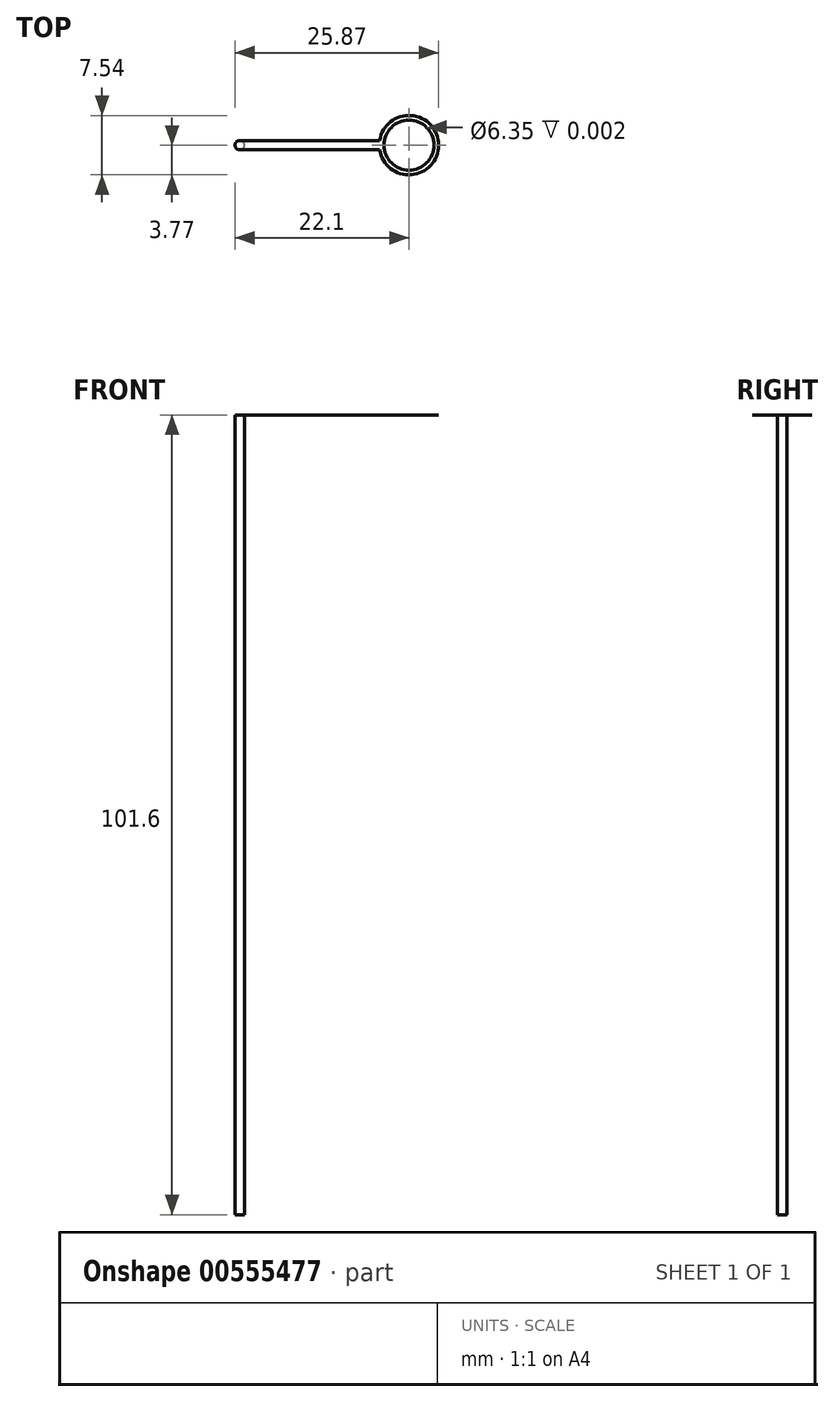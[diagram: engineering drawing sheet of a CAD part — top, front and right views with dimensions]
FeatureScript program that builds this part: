
annotation { "Feature Type Name" : "Feature", "Feature Type Description" : "" }
export const myFeature = defineFeature(function(context is Context, id is Id, definition is map)
    precondition{}
    {
        {
            var Q0;
            Q0=qCreatedBy(makeId("Top.planeOp"),FACE);
            var sketch = newSketch(context, id + "F0", { "sketchPlane" : qUnion([Q0])});
            skCircle(sketch, "E0", {"center": v(0, 0) * mm, "radius": 3.18 * mm});
            skCircle(sketch, "E1", {"center": v(0, 0) * mm, "radius": 3.77 * mm});
            skLineSegment(sketch, "E2", {"start": v(-21.5, 0.6) * mm, "end": v(-3.72, 0.6) * mm});
            skLineSegment(sketch, "E3", {"start": v(-21.5, -0.6) * mm, "end": v(-3.72, -0.6) * mm});
            skCircle(sketch, "E4", {"center": v(-21.5, 0) * mm, "radius": 0.6 * mm});
            skSolve(sketch);
        }
        {
            var Q0;
            {var subQ0=sQuery(id+"F0.wireOp",EDGE,"E2");Q0=makeQuery(id+"F0.imprint","IMPRINT",FACE,{"disambiguationData":[TD([[makeQuery(id+"F0.imprint","IMPRINT",EDGE,{"derivedFrom":subQ0}),-1.0]])]});}
            var Q1;
            Q1=makeQuery(id+"F0.imprint","IMPRINT",FACE,{"disambiguationData":[TD([[makeQuery(id+"F0.imprint","IMPRINT",EDGE,{"derivedFrom":sQuery(id+"F0.wireOp",EDGE,"E0")}),-1.0]])]});
            var Q2;
            {var subQ0=sQuery(id+"F0.wireOp",EDGE,"E4");var subQ1=makeQuery(id+"F0.imprint","INTERSECT",VERTEX,{"derivedFrom":[sQuery(id+"F0.wireOp",EDGE,"E2"),subQ0]});Q2=makeQuery(id+"F0.imprint","IMPRINT",FACE,{"disambiguationData":[TD([[makeQuery(id+"F0.imprint","IMPRINT",EDGE,{"disambiguationData":[TD([[subQ1,-1.0]])],"derivedFrom":subQ0}),1.0]])]});}
            extrude(context, id + "F1", {"entities" : qUnion([Q0, Q1, Q2]), "depth" : 3 / 1625.6 * mm, "offsetDistance" : 25.4 * mm});
        }
        {
            var Q0;
            {var subQ0=sQuery(id+"F0.wireOp",EDGE,"E4");var subQ1=makeQuery(id+"F0.imprint","INTERSECT",VERTEX,{"derivedFrom":[sQuery(id+"F0.wireOp",EDGE,"E2"),subQ0]});Q0=makeQuery(id+"F0.imprint","IMPRINT",FACE,{"disambiguationData":[TD([[makeQuery(id+"F0.imprint","IMPRINT",EDGE,{"disambiguationData":[TD([[subQ1,-1.0]])],"derivedFrom":subQ0}),1.0]])]});}
            var Q1;
            Q1=sQuery(id+"F0.wireOp",EDGE,"8kEqgfxY-QX5D-swLe-gkhk-hIvBlWavA6Kc");
            extrude(context, id + "F2", {"entities" : qUnion([Q0]), "operationType" : NewBodyOperationType.ADD, "surfaceEntities" : qUnion([Q1]), "oppositeDirection" : true, "depth" : 101.6 * mm, "offsetDistance" : 25.4 * mm});
        }
    });
